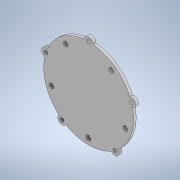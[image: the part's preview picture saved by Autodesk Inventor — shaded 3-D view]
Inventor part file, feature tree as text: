
AUTODESK INVENTOR PART (.ipt)
format: ipt  version: 2022 (Build 260153000, 153)  size: 151,040 bytes
history: native  units: mm
features: sketch x2, extrude x1
ambient origin geometry x8: Origin, YZ Plane, XZ Plane, XY Plane, X Axis, Y Axis, Z Axis, Center Point
bodies: Solid1 (feature_tree)
feature tree (3):
  sketch  "Sketch1"  dims[d0=98.0mm d2=5.4mm]
  extrude  "BaseSuelo"  Depth=5.4mm
  sketch  "Sketch2"  dims[d3=50.0mm d5=360.0deg d7=10.0mm d8=4.2mm d9=50.0mm d11=360.0deg d13=3.0mm d14=0.0mm d15=51.0mm]
